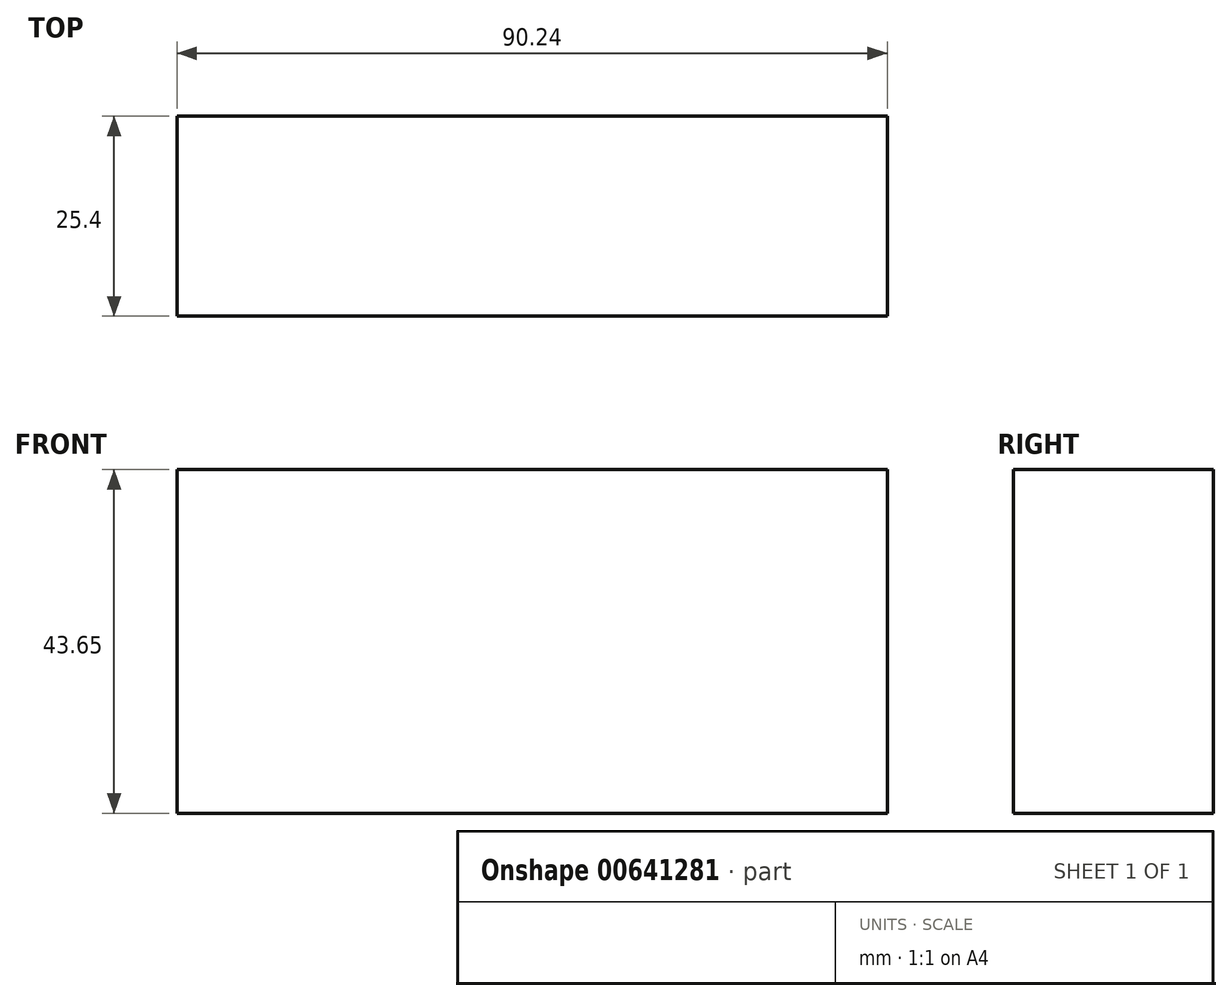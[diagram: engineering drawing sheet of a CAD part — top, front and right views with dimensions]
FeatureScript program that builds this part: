
annotation { "Feature Type Name" : "Feature", "Feature Type Description" : "" }
export const myFeature = defineFeature(function(context is Context, id is Id, definition is map)
    precondition{}
    {
        {
            var Q0;
            Q0=qCreatedBy(makeId("Front.planeOp"),FACE);
            var sketch = newSketch(context, id + "F0", { "sketchPlane" : qUnion([Q0])});
            skLineSegment(sketch, "E0.bottom", {"start": v(45.52, 0) * mm, "end": v(-44.72, 0) * mm});
            skLineSegment(sketch, "E0.top", {"start": v(45.52, 43.65) * mm, "end": v(-44.72, 43.65) * mm});
            skLineSegment(sketch, "E0.left", {"start": v(45.52, 0) * mm, "end": v(45.52, 43.65) * mm});
            skLineSegment(sketch, "E0.right", {"start": v(-44.72, 0) * mm, "end": v(-44.72, 43.65) * mm});
            skSolve(sketch);
        }
        {
            var Q0;
            Q0=makeQuery(id+"F0.imprint","IMPRINT",FACE,{"disambiguationData":[TD([[makeQuery(id+"F0.imprint","IMPRINT",EDGE,{"derivedFrom":sQuery(id+"F0.wireOp",EDGE,"E0.bottom")}),-1.0]])]});
            extrude(context, id + "F1", {"entities" : qUnion([Q0]), "oppositeDirection" : true, "depth" : 25.4 * mm, "offsetDistance" : 25.4 * mm});
        }
    });
